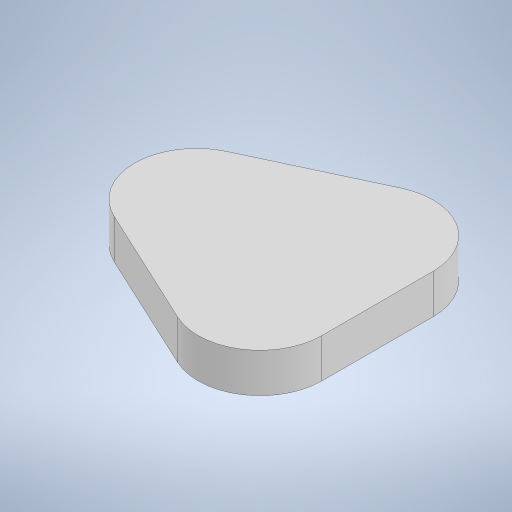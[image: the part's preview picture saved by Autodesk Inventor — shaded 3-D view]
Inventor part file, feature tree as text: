
AUTODESK INVENTOR PART (.ipt)
format: ipt  version: 2024.3 (Build 283343000, 343)  size: 282,624 bytes
history: native  units: in
note: dims shown in document units (in); Inventor stores cm internally (conversion verified against a paired STEP export)
features: extrude x4, sketch x4, projected_geometry x2
ambient origin geometry x8: Origin, YZ Plane, XZ Plane, XY Plane, X Axis, Y Axis, Z Axis, Center Point
bodies: Solid1 (feature_tree)
feature tree (10):
  extrude  "Extrusion1"  Depth=0.8583in
  extrude  "Extrusion2"  Depth=0.0394in
  extrude  "Extrusion3"  Depth=0.8926in
  extrude  "Extrusion4"  Depth=0.2008in TaperAngle=0.0deg
  sketch  "Sketch1"  dims[d0=0.3436in d1=0.8583in d2=1.2874in d3=0.8583in d4=0.8583in]
  sketch  "Sketch2"  dims[d5=0.0394in d6=0.0in d7=0.8926in]
  projected_geometry  "Projected Loop1"
  sketch  "Sketch3"  dims[d8=0.8926in d9=0.8926in]
  projected_geometry  "Projected Loop2"
  sketch  "Sketch4"  dims[d10=0.0394in d11=0.0in d15=0.2008in d16=0.0in d17=0.0433in d18=0.2047in d19=0.0433in d20=0.0in]
